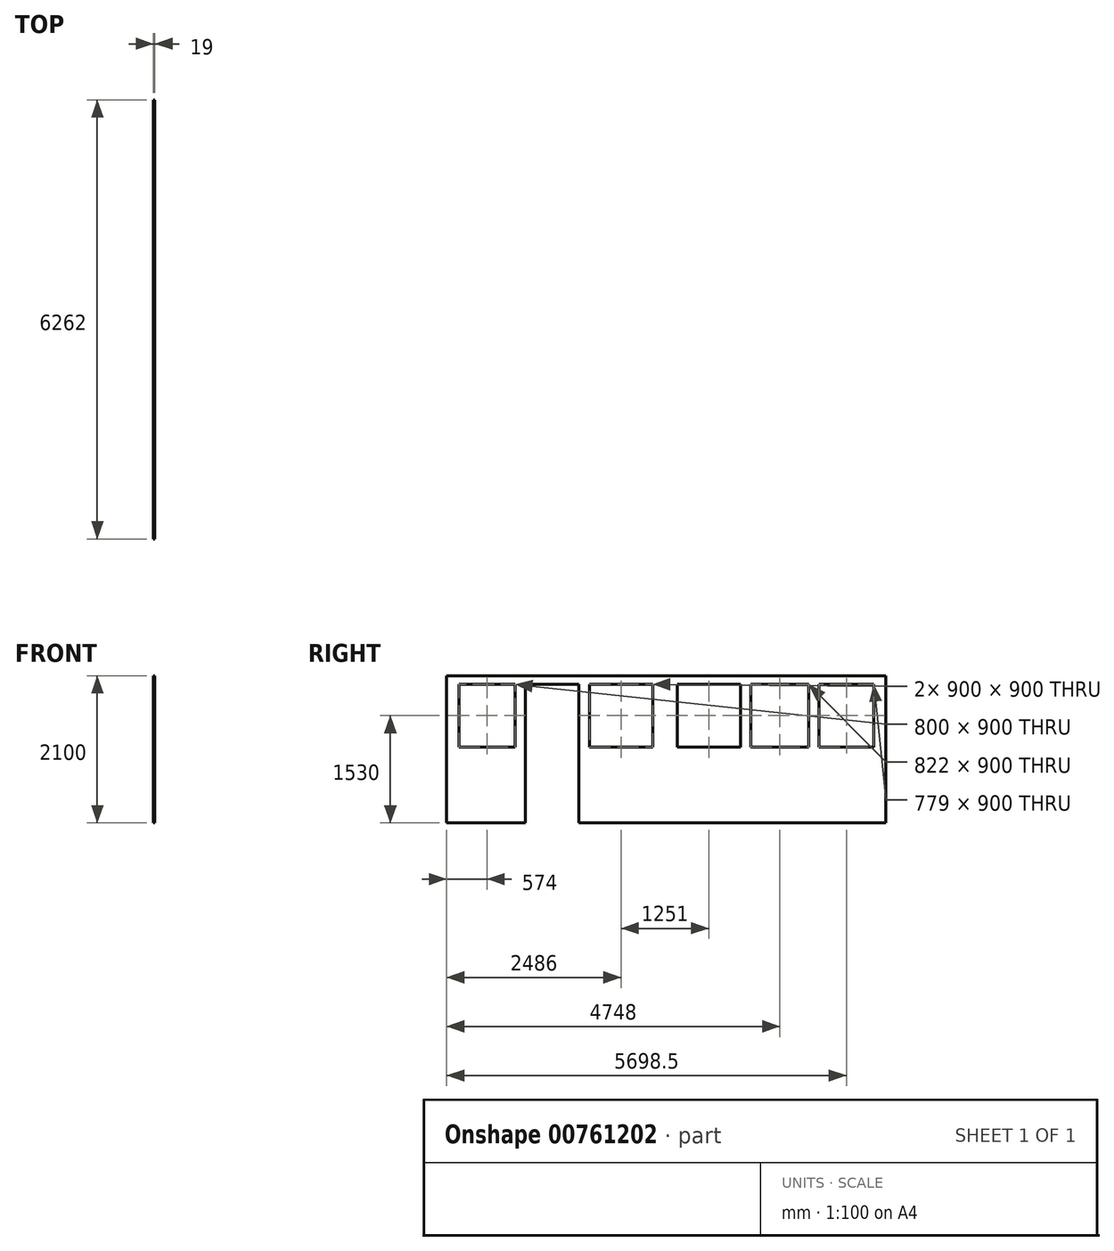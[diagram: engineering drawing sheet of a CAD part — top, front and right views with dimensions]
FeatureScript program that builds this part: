
annotation { "Feature Type Name" : "Feature", "Feature Type Description" : "" }
export const myFeature = defineFeature(function(context is Context, id is Id, definition is map)
    precondition{}
    {
        {
            var Q0;
            Q0=qCreatedBy(makeId("Right.planeOp"),FACE);
            var sketch = newSketch(context, id + "F0", { "sketchPlane" : qUnion([Q0])});
            skLineSegment(sketch, "E0.bottom", {"start": v(0, 0) * mm, "end": v(1124, 0) * mm});
            skLineSegment(sketch, "E0.top", {"start": v(0, 2100) * mm, "end": v(6262, 2100) * mm});
            skLineSegment(sketch, "E0.left", {"start": v(0, 0) * mm, "end": v(0, 2100) * mm});
            skLineSegment(sketch, "E0.right", {"start": v(6262, 0) * mm, "end": v(6262, 2100) * mm});
            skLineSegment(sketch, "E1.top", {"start": v(1124, 1980) * mm, "end": v(1886, 1980) * mm});
            skLineSegment(sketch, "E1.left", {"start": v(1124, 0) * mm, "end": v(1124, 1980) * mm});
            skLineSegment(sketch, "E1.right", {"start": v(1886, 0) * mm, "end": v(1886, 1980) * mm});
            skLineSegment(sketch, "E2.bottom", {"start": v(174, 1980) * mm, "end": v(974, 1980) * mm});
            skLineSegment(sketch, "E2.top", {"start": v(174, 1080) * mm, "end": v(974, 1080) * mm});
            skLineSegment(sketch, "E2.left", {"start": v(174, 1980) * mm, "end": v(174, 1080) * mm});
            skLineSegment(sketch, "E2.right", {"start": v(974, 1980) * mm, "end": v(974, 1080) * mm});
            skPoint(sketch, "E3.oppositeSnap0", {"position": v(1514, 1080) * mm});
            skLineSegment(sketch, "E3.bottom", {"start": v(2036, 1980) * mm, "end": v(2936, 1980) * mm});
            skLineSegment(sketch, "E3.top", {"start": v(2036, 1080) * mm, "end": v(2936, 1080) * mm});
            skLineSegment(sketch, "E3.left", {"start": v(2036, 1980) * mm, "end": v(2036, 1080) * mm});
            skLineSegment(sketch, "E3.right", {"start": v(2936, 1980) * mm, "end": v(2936, 1080) * mm});
            skLineSegment(sketch, "E4.bottom", {"start": v(3287, 1980) * mm, "end": v(4187, 1980) * mm});
            skLineSegment(sketch, "E4.top", {"start": v(3287, 1080) * mm, "end": v(4187, 1080) * mm});
            skLineSegment(sketch, "E4.left", {"start": v(3287, 1980) * mm, "end": v(3287, 1080) * mm});
            skLineSegment(sketch, "E4.right", {"start": v(4187, 1980) * mm, "end": v(4187, 1080) * mm});
            skLineSegment(sketch, "E5.bottom", {"start": v(4337, 1980) * mm, "end": v(5159, 1980) * mm});
            skLineSegment(sketch, "E5.top", {"start": v(4337, 1080) * mm, "end": v(5159, 1080) * mm});
            skLineSegment(sketch, "E5.left", {"start": v(4337, 1980) * mm, "end": v(4337, 1080) * mm});
            skLineSegment(sketch, "E5.right", {"start": v(5159, 1980) * mm, "end": v(5159, 1080) * mm});
            skPoint(sketch, "E6.firstSnap0", {"position": v(1871, 1980) * mm});
            skLineSegment(sketch, "E6.bottom", {"start": v(5309, 1980) * mm, "end": v(6088, 1980) * mm});
            skLineSegment(sketch, "E6.top", {"start": v(5309, 1080) * mm, "end": v(6088, 1080) * mm});
            skLineSegment(sketch, "E6.left", {"start": v(5309, 1980) * mm, "end": v(5309, 1080) * mm});
            skLineSegment(sketch, "E6.right", {"start": v(6088, 1980) * mm, "end": v(6088, 1080) * mm});
            skLineSegment(sketch, "E7.trimOffspring", {"start": v(1886, 0) * mm, "end": v(6262, 0) * mm});
            skSolve(sketch);
        }
        {
            var Q0;
            Q0 = qSketchRegion(id + "F0", true);
            extrude(context, id + "F1", {"entities" : qUnion([Q0]), "depth" : 19 * mm, "offsetDistance" : 25 * mm});
        }
    });
